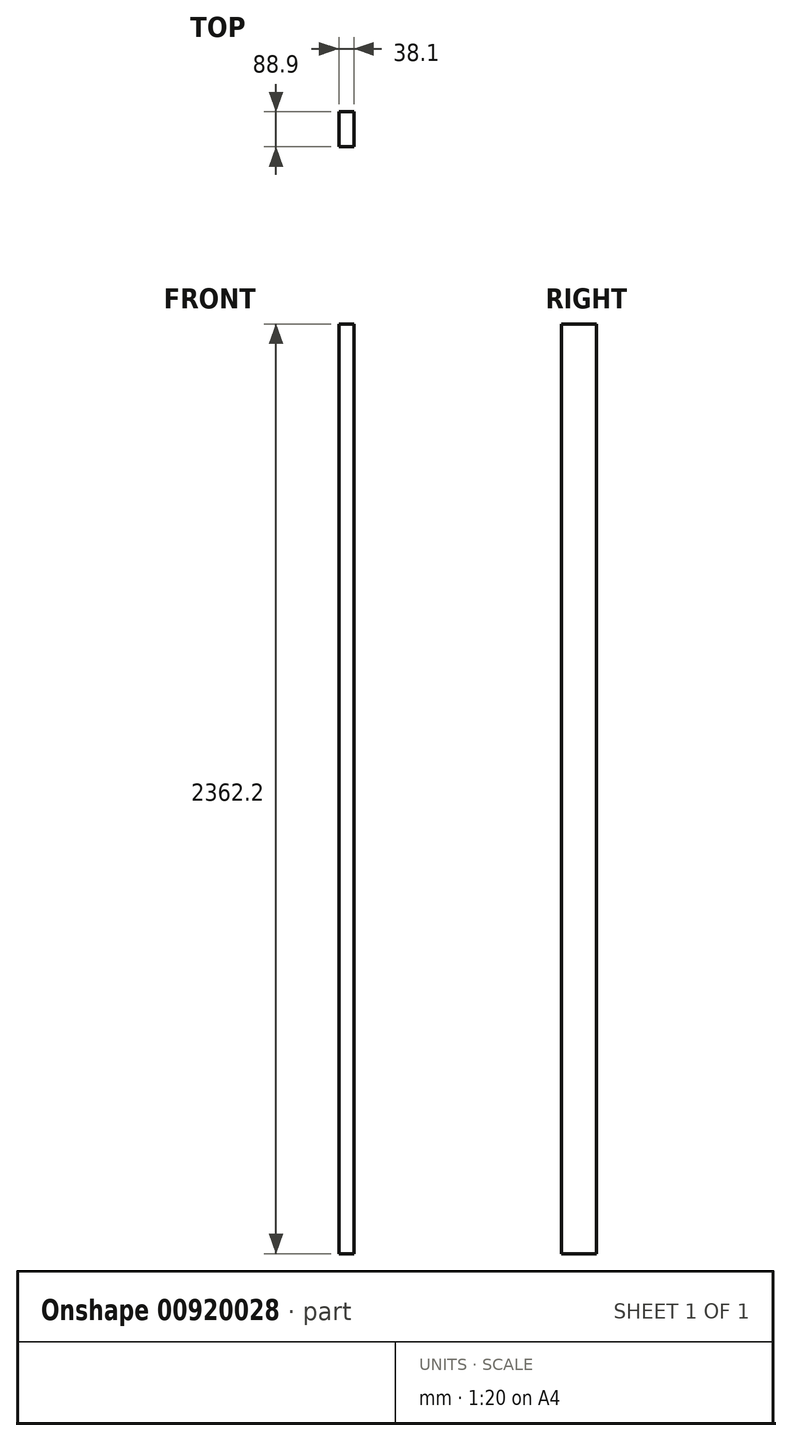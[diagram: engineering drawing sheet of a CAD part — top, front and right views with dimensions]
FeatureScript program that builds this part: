
annotation { "Feature Type Name" : "Feature", "Feature Type Description" : "" }
export const myFeature = defineFeature(function(context is Context, id is Id, definition is map)
    precondition{}
    {
        {
            var Q0;
            Q0=qCreatedBy(makeId("Top.planeOp"),FACE);
            var sketch = newSketch(context, id + "F0", { "sketchPlane" : qUnion([Q0])});
            skLineSegment(sketch, "E0.bottom", {"start": v(19.05, 44.45) * mm, "end": v(-19.05, 44.45) * mm});
            skLineSegment(sketch, "E0.top", {"start": v(19.05, -44.45) * mm, "end": v(-19.05, -44.45) * mm});
            skLineSegment(sketch, "E0.left", {"start": v(19.05, 44.45) * mm, "end": v(19.05, -44.45) * mm});
            skLineSegment(sketch, "E0.right", {"start": v(-19.05, 44.45) * mm, "end": v(-19.05, -44.45) * mm});
            skPoint(sketch, "E0.middle", {"position": v(0, 0) * mm});
            skSolve(sketch);
        }
        {
            var Q0;
            Q0 = qSketchRegion(id + "F0", true);
            extrude(context, id + "F1", {"entities" : qUnion([Q0]), "depth" : 2362.2 * mm, "offsetDistance" : 25.4 * mm});
        }
    });
